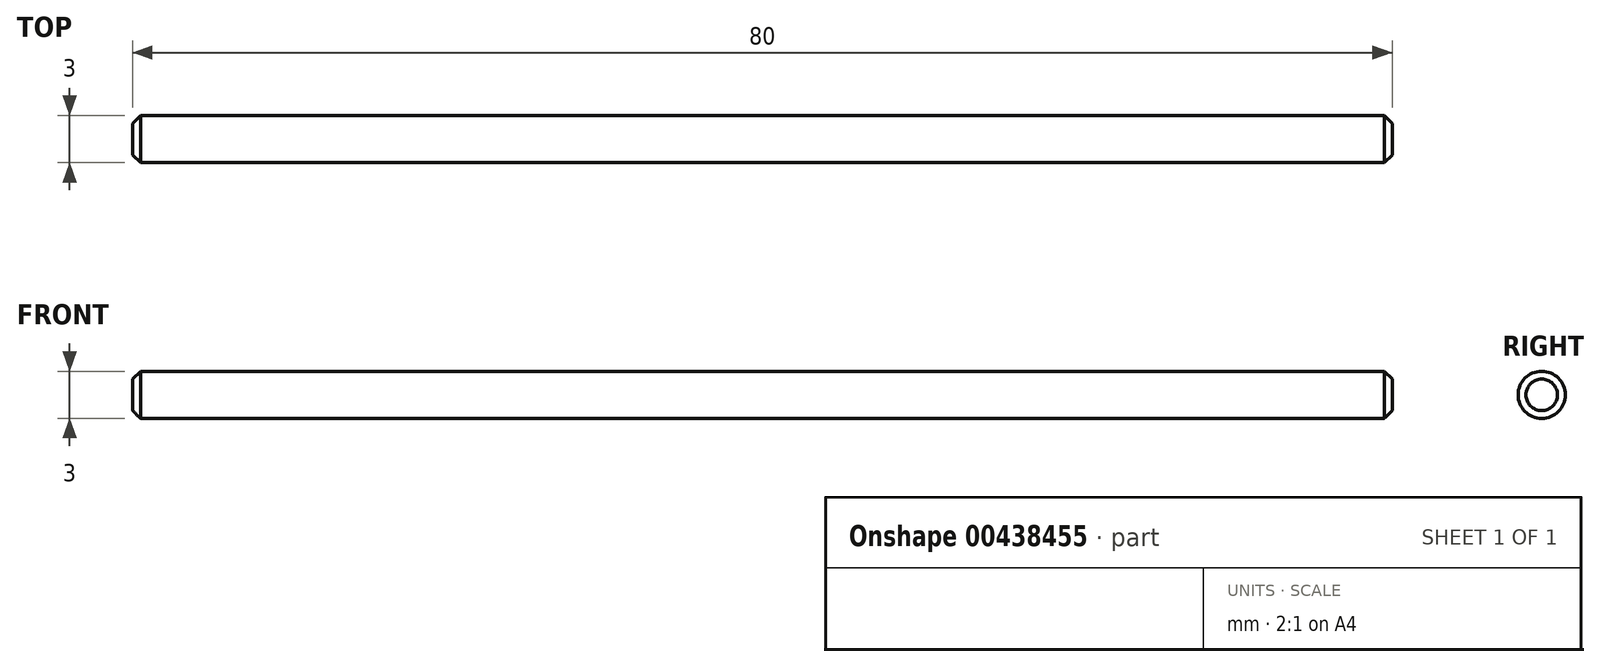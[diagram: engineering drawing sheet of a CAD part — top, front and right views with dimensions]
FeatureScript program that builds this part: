
annotation { "Feature Type Name" : "Feature", "Feature Type Description" : "" }
export const myFeature = defineFeature(function(context is Context, id is Id, definition is map)
    precondition{}
    {
        {
            var Q0;
            Q0=qCreatedBy(makeId("Right.planeOp"),FACE);
            var sketch = newSketch(context, id + "F0", { "sketchPlane" : qUnion([Q0])});
            skCircle(sketch, "E0", {"center": v(0, 0) * mm, "radius": 1.5 * mm});
            skSolve(sketch);
        }
        {
            var Q0;
            Q0=makeQuery(id+"F0.imprint","IMPRINT",FACE,{"disambiguationData":[TD([[makeQuery(id+"F0.imprint","IMPRINT",EDGE,{"derivedFrom":sQuery(id+"F0.wireOp",EDGE,"E0")}),1.0]])]});
            extrude(context, id + "F1", {"entities" : qUnion([Q0]), "depth" : 80 * mm});
        }
        {
            var Q0;
            Q0=makeQuery(id+"F1.opExtrude","CAP_EDGE",EDGE,{"disambiguationData":[OSD([sQuery(id+"F0.wireOp",EDGE,"E0")])],"isStart":false});
            var Q1;
            Q1=makeQuery(id+"F1.opExtrude","CAP_FACE",FACE,{"disambiguationData":[OSD([sQuery(id+"F0.wireOp",EDGE,"E0")])],"isStart":true});
            chamfer(context, id + "F2", {"entities" : qUnion([Q0, Q1]), "width" : 0.5 * mm, "tangentPropagation" : true});
        }
    });
